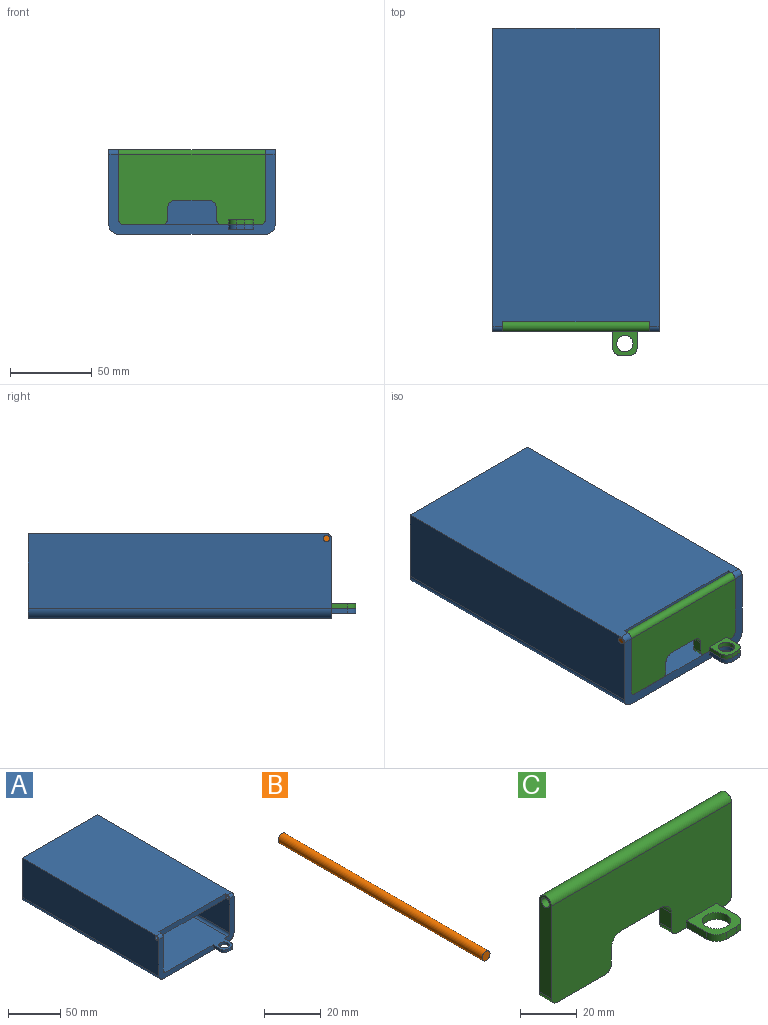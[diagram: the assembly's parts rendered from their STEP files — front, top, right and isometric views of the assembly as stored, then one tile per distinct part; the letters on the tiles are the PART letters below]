
ASSEMBLY  parts=3 mates=1
PART A: 27 faces, bbox 102x201x52 mm
  f0: plane 195x84mm, normal (0,0,1), area 15255.7mm2, adj f1,f3,f12,f13,f15,f16,f23,f24
  f1: plane 10x3mm, normal (-1,0,0), area 30mm2, adj f0,f2,f15,f25
  f2: plane 15x15mm, normal (0,0,-1), area 135.7mm2, adj f1,f3,f15,f23,f24,f25,f26
  f3: plane 5x3mm, normal (0,-1,0), area 15mm2, adj f0,f2,f25,f26
  f4: plane 174x90mm, normal (0,0,-1), area 15660mm2, adj f10,f11,f16,f18
  f5: plane 183x102mm, normal (0,0,1), area 18396mm2, adj f6,f10,f11,f14,f17,f18,f21,f22
  f6: plane 186x46mm, normal (-1,0,0), area 8541.5mm2, adj f5,f7,f15,f17,f20,f22
  f7: cylinder r=6mm len=186mm, axis (0,1,0), area 1753mm2, adj f6,f8,f15,f17
  f8: plane 186x90mm, normal (0,0,-1), area 16740mm2, adj f7,f9,f15,f17
  f9: cylinder r=6mm len=186mm, axis (0,1,0), area 1753mm2, adj f8,f14,f15,f17
  f10: plane 180x43mm, normal (1,0,0), area 6681.5mm2, adj f4,f5,f13,f15,f16,f18,f20,f22
  f11: plane 180x43mm, normal (-1,0,0), area 6681.5mm2, adj f4,f5,f12,f15,f16,f18,f19,f21
  f12: cylinder r=3mm len=180mm, axis (0,1,0), area 848.2mm2, adj f0,f11,f15,f16
  f13: cylinder r=3mm len=180mm, axis (0,1,0), area 848.2mm2, adj f0,f10,f15,f16
  f14: plane 186x46mm, normal (1,0,0), area 8541.5mm2, adj f5,f9,f15,f17,f19,f21
  f15: plane 102x49mm, normal (0,-1,0), area 1071.4mm2, adj f0,f1,f2,f6,f7,f8,f9,f10
  f16: plane 90x40mm, normal (0,-1,0), area 3596.1mm2, adj f0,f4,f10,f11,f12,f13
  f17: plane 102x52mm, normal (0,1,0), area 5288.5mm2, adj f5,f6,f7,f8,f9,f14
  f18: plane 90x6mm, normal (0,-1,0), area 540mm2, adj f4,f5,f10,f11
  f19: cylinder r=2mm len=6mm, axis (1,0,0), area 75.4mm2, adj f11,f14
  f20: cylinder r=2mm len=6mm, axis (1,0,0), area 75.4mm2, adj f6,f10
  f21: cylinder r=3mm len=6mm, axis (1,0,0), area 28.3mm2, adj f5,f11,f14,f15
  f22: cylinder r=3mm len=6mm, axis (1,0,0), area 28.3mm2, adj f5,f6,f10,f15
  f23: plane 10x3mm, normal (1,0,0), area 30mm2, adj f0,f2,f15,f26
  f24: cylinder r=5mm len=10mm, axis (0,0,1), area 94.2mm2, adj f0,f2
  f25: cylinder r=5mm len=5mm, axis (0,0,1), area 23.6mm2, adj f0,f1,f2,f3
  f26: cylinder r=5mm len=5mm, axis (0,0,1), area 23.6mm2, adj f0,f2,f3,f23
PART B: 3 faces, bbox 4x102x4 mm
  f0: cylinder r=2mm len=102mm, axis (0,1,0), area 1281.8mm2, adj f1,f2
  f1: plane 4x4mm, normal (0,-1,0), area 12.6mm2, adj f0
  f2: plane 4x4mm, normal (0,1,0), area 12.6mm2, adj f0
PART C: 24 faces, bbox 90x21x46 mm
  f0: plane 24x21mm, normal (0,0,-1), area 279.7mm2, adj f2,f3,f12,f14,f15,f19,f20,f21
  f1: plane 15x15mm, normal (0,0,1), area 135.7mm2, adj f2,f3,f19,f20,f21,f22,f23
  f2: plane 5x3mm, normal (0,-1,0), area 15mm2, adj f0,f1,f22,f23
  f3: plane 90x43mm, normal (0,-1,0), area 3378mm2, adj f0,f1,f4,f5,f6,f7,f8,f9
  f4: plane 7x6mm, normal (1,0,0), area 42mm2, adj f3,f5,f12,f17
  f5: cylinder r=5mm len=6mm, axis (0,1,0), area 47.1mm2, adj f3,f4,f6,f12
  f6: plane 20x6mm, normal (0,0,-1), area 120mm2, adj f3,f5,f7,f12
  f7: cylinder r=5mm len=6mm, axis (0,1,0), area 47.1mm2, adj f3,f6,f8,f12
  f8: plane 7x6mm, normal (-1,0,0), area 42mm2, adj f3,f7,f12,f14
  f9: plane 43x6mm, normal (1,0,0), area 241.6mm2, adj f3,f12,f13,f15,f18
  f10: plane 43x6mm, normal (-1,0,0), area 241.6mm2, adj f3,f12,f13,f16,f18
  f11: plane 24x6mm, normal (0,0,-1), area 144mm2, adj f3,f12,f16,f17
  f12: plane 90x43mm, normal (0,1,0), area 3423mm2, adj f0,f4,f5,f6,f7,f8,f9,f10
  f13: cylinder r=2mm len=90mm, axis (1,0,0), area 1131mm2, adj f9,f10
  f14: cylinder r=3mm len=6mm, axis (0,1,0), area 28.3mm2, adj f0,f3,f8,f12
  f15: cylinder r=3mm len=6mm, axis (0,-1,0), area 28.3mm2, adj f0,f3,f9,f12
  f16: cylinder r=3mm len=6mm, axis (0,1,0), area 28.3mm2, adj f3,f10,f11,f12
  f17: cylinder r=3mm len=6mm, axis (0,-1,0), area 28.3mm2, adj f3,f4,f11,f12
  f18: cylinder r=3mm len=90mm, axis (1,0,0), area 848.2mm2, adj f3,f9,f10,f12
  f19: plane 10x3mm, normal (-1,0,0), area 30mm2, adj f0,f1,f3,f22
  f20: plane 10x3mm, normal (1,0,0), area 30mm2, adj f0,f1,f3,f23
  f21: cylinder r=5mm len=10mm, axis (0,0,1), area 94.2mm2, adj f0,f1
  f22: cylinder r=5mm len=5mm, axis (0,0,1), area 23.6mm2, adj f0,f1,f2,f19
  f23: cylinder r=5mm len=5mm, axis (0,0,1), area 23.6mm2, adj f0,f1,f2,f20
PLACE A t=(-29.5,-9.98,15.08)mm
PLACE B rot(axis=(-0.58,0.58,0.58),120deg) t=(-29.5,-96.98,38.08)mm
PLACE C t=(-29.5,-96.98,18.08)mm
MATE fastened B.f0 <-> A.f19  axis (1,0,0) through (21.5,-96.98,38.08)mm
